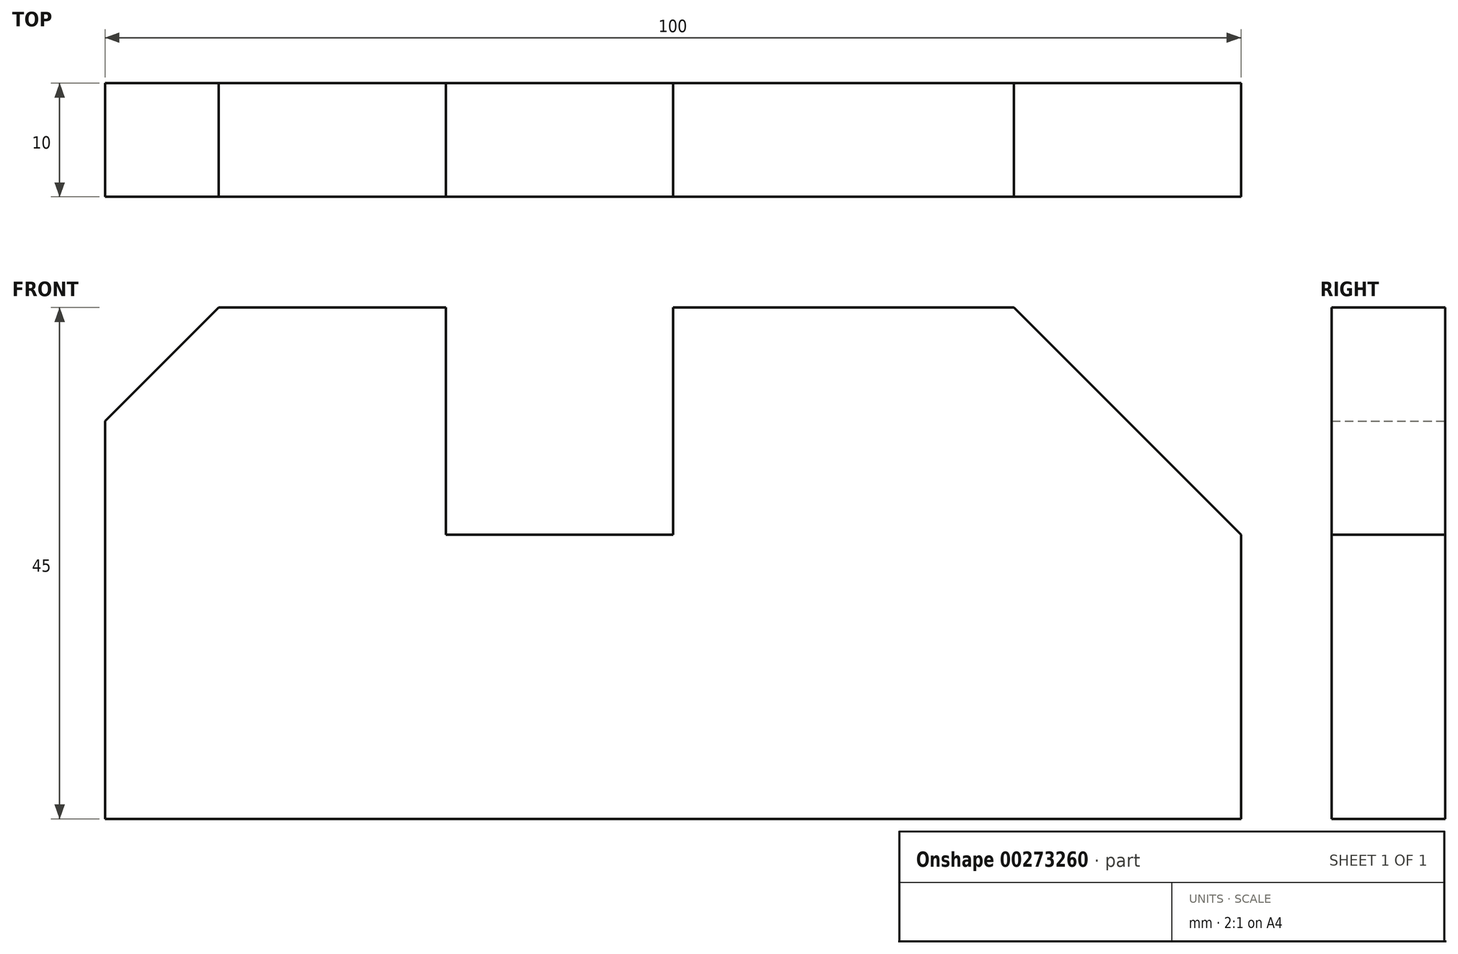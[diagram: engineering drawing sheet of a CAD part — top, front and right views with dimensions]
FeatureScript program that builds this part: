
annotation { "Feature Type Name" : "Feature", "Feature Type Description" : "" }
export const myFeature = defineFeature(function(context is Context, id is Id, definition is map)
    precondition{}
    {
        {
            var Q0;
            Q0=qCreatedBy(makeId("Front.planeOp"),FACE);
            var sketch = newSketch(context, id + "F0", { "sketchPlane" : qUnion([Q0])});
            skLineSegment(sketch, "E0", {"start": v(0, 0) * mm, "end": v(100, 0) * mm});
            skLineSegment(sketch, "E1", {"start": v(100, 0) * mm, "end": v(100, 25) * mm});
            skLineSegment(sketch, "E2", {"start": v(10, 45) * mm, "end": v(0, 35) * mm});
            skLineSegment(sketch, "E3", {"start": v(10, 45) * mm, "end": v(30, 45) * mm});
            skLineSegment(sketch, "E4", {"start": v(30, 45) * mm, "end": v(30, 25) * mm});
            skLineSegment(sketch, "E5", {"start": v(30, 25) * mm, "end": v(50, 25) * mm});
            skLineSegment(sketch, "E6", {"start": v(50, 25) * mm, "end": v(50, 45) * mm});
            skLineSegment(sketch, "E7", {"start": v(50, 45) * mm, "end": v(80, 45) * mm});
            skLineSegment(sketch, "E8", {"start": v(80, 45) * mm, "end": v(100, 25) * mm});
            skLineSegment(sketch, "E9", {"start": v(0, 35) * mm, "end": v(0, 0) * mm});
            skSolve(sketch);
        }
        {
            var Q0;
            Q0=makeQuery(id+"F0.imprint","IMPRINT",FACE,{"disambiguationData":[TD([[makeQuery(id+"F0.imprint","IMPRINT",EDGE,{"derivedFrom":sQuery(id+"F0.wireOp",EDGE,"E0")}),1.0]])]});
            extrude(context, id + "F1", {"entities" : qUnion([Q0]), "depth" : 10 * mm});
        }
    });
